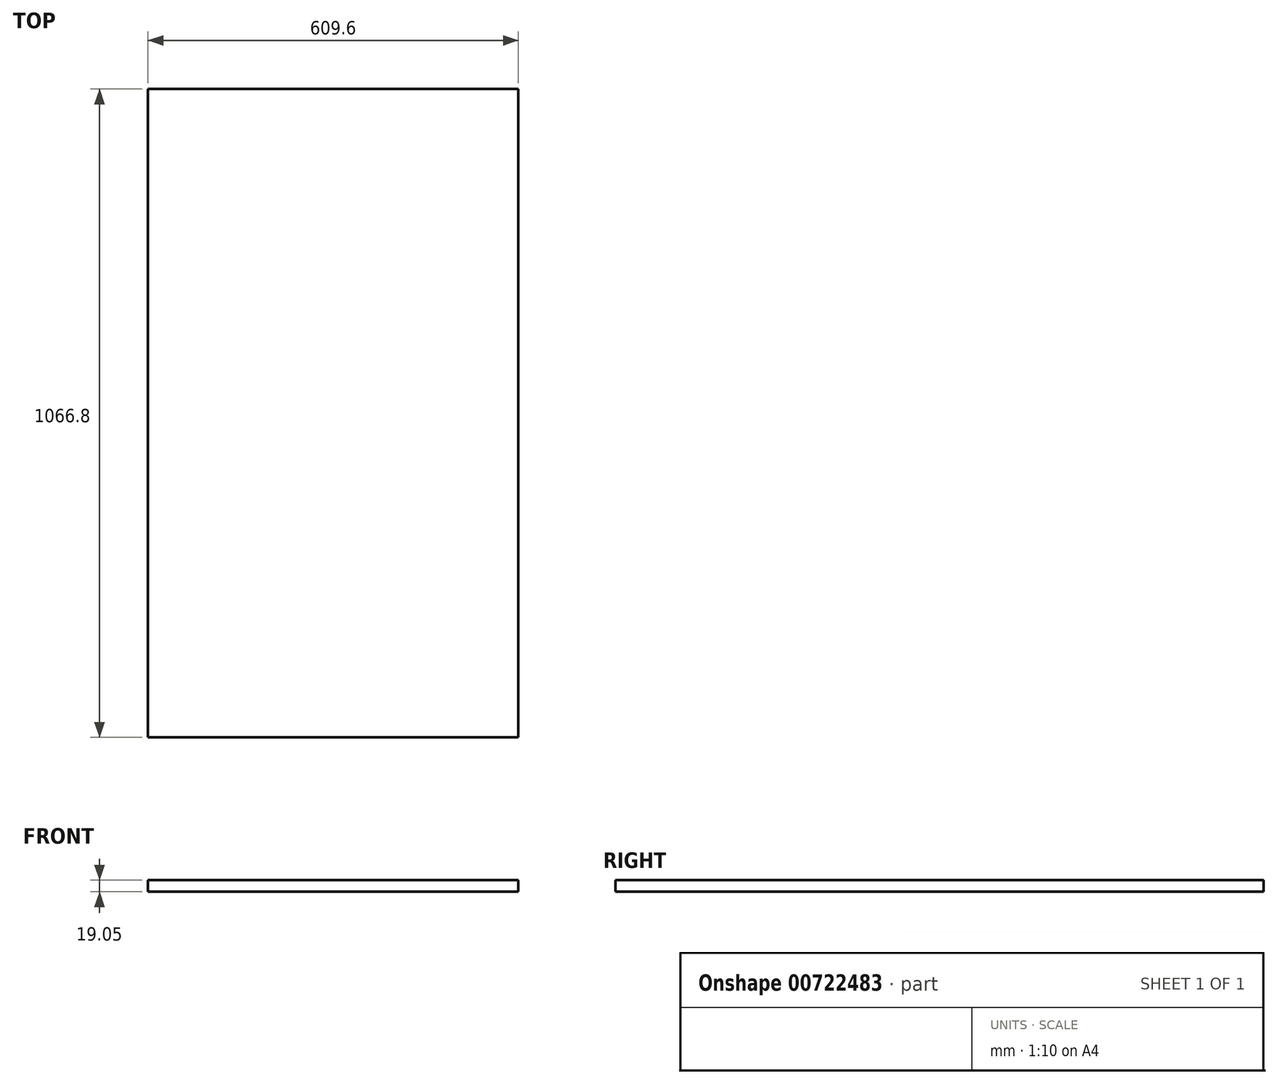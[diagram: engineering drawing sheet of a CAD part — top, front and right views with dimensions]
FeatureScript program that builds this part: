
annotation { "Feature Type Name" : "Feature", "Feature Type Description" : "" }
export const myFeature = defineFeature(function(context is Context, id is Id, definition is map)
    precondition{}
    {
        {
            var Q0;
            Q0=qCreatedBy(makeId("Top.planeOp"),FACE);
            var sketch = newSketch(context, id + "F0", { "sketchPlane" : qUnion([Q0])});
            skLineSegment(sketch, "E0.bottom", {"start": v(0, 0) * mm, "end": v(609.6, 0) * mm});
            skLineSegment(sketch, "E0.top", {"start": v(0, -1066.8) * mm, "end": v(609.6, -1066.8) * mm});
            skLineSegment(sketch, "E0.left", {"start": v(0, 0) * mm, "end": v(0, -1066.8) * mm});
            skLineSegment(sketch, "E0.right", {"start": v(609.6, 0) * mm, "end": v(609.6, -1066.8) * mm});
            skSolve(sketch);
        }
        {
            var Q0;
            Q0=makeQuery(id+"F0.imprint","IMPRINT",FACE,{"disambiguationData":[TD([[makeQuery(id+"F0.imprint","IMPRINT",EDGE,{"derivedFrom":sQuery(id+"F0.wireOp",EDGE,"E0.bottom")}),-1.0]])]});
            extrude(context, id + "F1", {"entities" : qUnion([Q0]), "oppositeDirection" : true, "depth" : 19.05 * mm, "offsetDistance" : 25.4 * mm});
        }
    });
